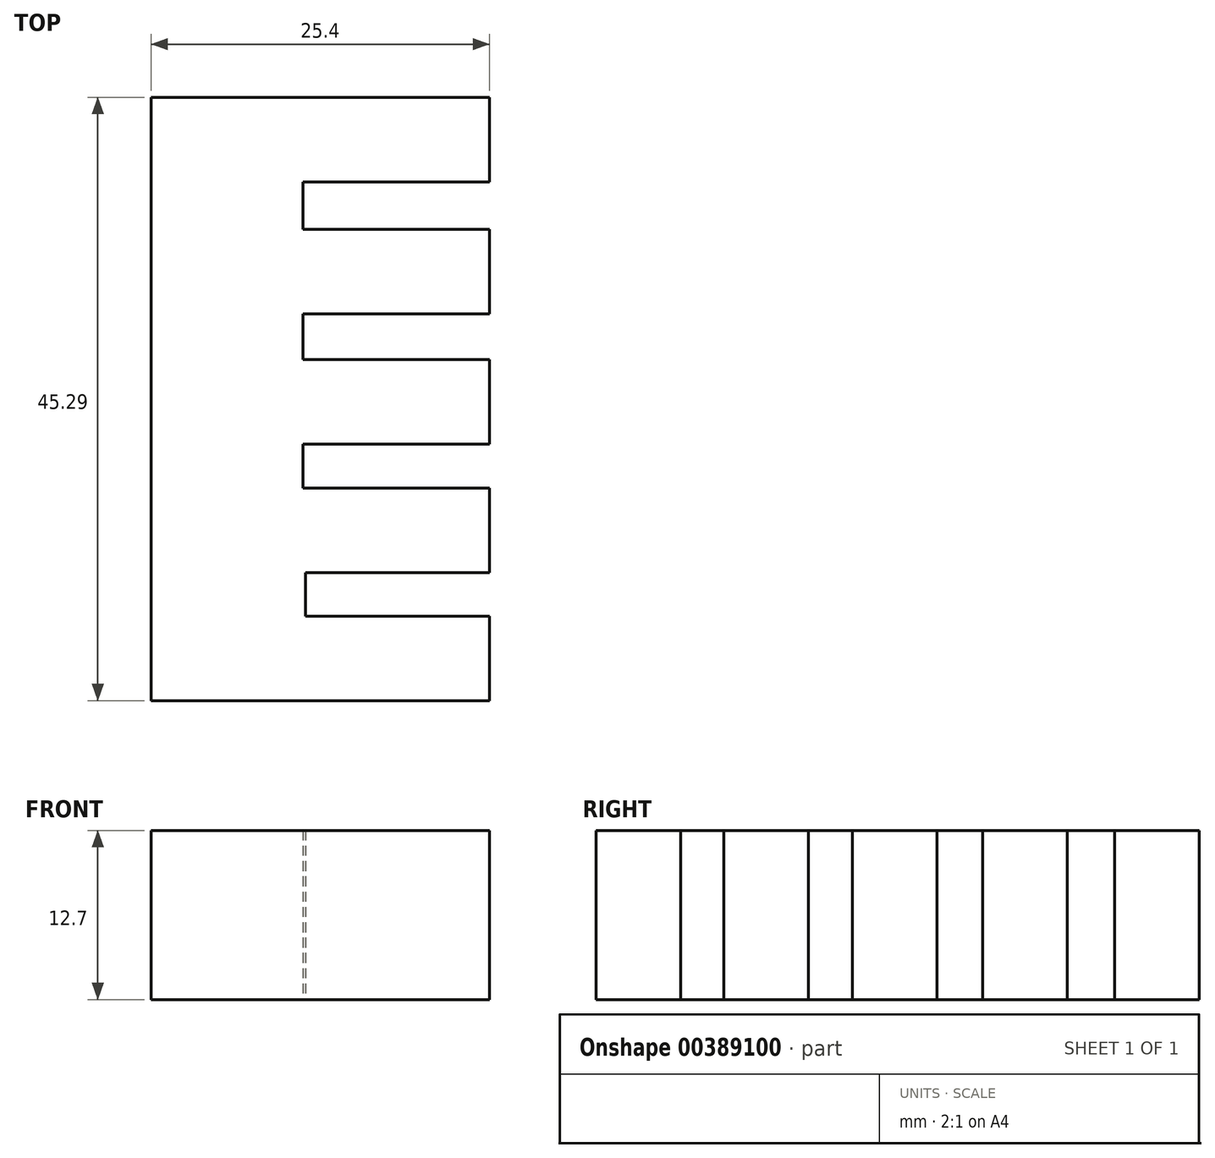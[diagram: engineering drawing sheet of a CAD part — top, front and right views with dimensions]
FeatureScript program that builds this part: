
annotation { "Feature Type Name" : "Feature", "Feature Type Description" : "" }
export const myFeature = defineFeature(function(context is Context, id is Id, definition is map)
    precondition{}
    {
        {
            var Q0;
            Q0=qCreatedBy(makeId("Top.planeOp"),FACE);
            var sketch = newSketch(context, id + "F0", { "sketchPlane" : qUnion([Q0])});
            skLineSegment(sketch, "E0", {"start": v(0, 0) * mm, "end": v(25.4, 0) * mm});
            skLineSegment(sketch, "E1", {"start": v(25.4, 0) * mm, "end": v(25.4, 6.35) * mm});
            skLineSegment(sketch, "E2", {"start": v(25.4, 6.35) * mm, "end": v(11.6, 6.35) * mm});
            skLineSegment(sketch, "E3", {"start": v(11.6, 6.35) * mm, "end": v(11.6, 9.6) * mm});
            skLineSegment(sketch, "E4", {"start": v(11.6, 9.6) * mm, "end": v(25.4, 9.6) * mm});
            skLineSegment(sketch, "E5", {"start": v(25.4, 9.6) * mm, "end": v(25.4, 15.95) * mm});
            skLineSegment(sketch, "E6", {"start": v(0, 16.13) * mm, "end": v(0, 0) * mm});
            skLineSegment(sketch, "E7", {"start": v(25.4, 15.95) * mm, "end": v(11.4, 15.95) * mm});
            skLineSegment(sketch, "E8", {"start": v(11.4, 15.95) * mm, "end": v(11.4, 19.25) * mm});
            skLineSegment(sketch, "E9", {"start": v(11.4, 19.25) * mm, "end": v(25.4, 19.25) * mm});
            skLineSegment(sketch, "E10", {"start": v(25.4, 19.25) * mm, "end": v(25.4, 25.6) * mm});
            skLineSegment(sketch, "E11", {"start": v(25.4, 25.6) * mm, "end": v(11.4, 25.6) * mm});
            skLineSegment(sketch, "E12", {"start": v(11.4, 25.6) * mm, "end": v(11.4, 29.03) * mm});
            skLineSegment(sketch, "E13", {"start": v(11.4, 29.03) * mm, "end": v(25.4, 29.03) * mm});
            skLineSegment(sketch, "E14", {"start": v(25.4, 29.03) * mm, "end": v(25.4, 35.38) * mm});
            skLineSegment(sketch, "E15", {"start": v(0, 35.38) * mm, "end": v(0, 16.13) * mm});
            skLineSegment(sketch, "E16", {"start": v(25.4, 35.38) * mm, "end": v(11.4, 35.38) * mm});
            skLineSegment(sketch, "E17", {"start": v(11.4, 35.38) * mm, "end": v(11.4, 38.94) * mm});
            skLineSegment(sketch, "E18", {"start": v(11.4, 38.94) * mm, "end": v(25.4, 38.94) * mm});
            skLineSegment(sketch, "E19", {"start": v(25.4, 38.94) * mm, "end": v(25.4, 45.29) * mm});
            skLineSegment(sketch, "E20", {"start": v(25.4, 45.29) * mm, "end": v(0, 45.29) * mm});
            skLineSegment(sketch, "E21", {"start": v(0, 35.38) * mm, "end": v(0, 45.29) * mm});
            skSolve(sketch);
        }
        {
            var Q0;
            Q0=makeQuery(id+"F0.imprint","IMPRINT",FACE,{"disambiguationData":[TD([[makeQuery(id+"F0.imprint","IMPRINT",EDGE,{"derivedFrom":sQuery(id+"F0.wireOp",EDGE,"E0")}),1.0]])]});
            extrude(context, id + "F1", {"entities" : qUnion([Q0]), "depth" : 12.7 * mm});
        }
    });
